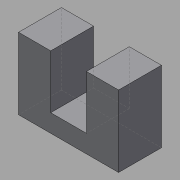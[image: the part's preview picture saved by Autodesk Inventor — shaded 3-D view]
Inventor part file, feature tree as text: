
AUTODESK INVENTOR PART (.ipt)
format: ipt  version: 2015 (Build 190159000, 159)  size: 77,312 bytes
history: native  units: in
note: dims shown in document units (in); Inventor stores cm internally (conversion verified against a paired STEP export)
features: other x3, sketch x2
ambient origin geometry x8: Origin, YZ Plane, XZ Plane, XY Plane, X Axis, Y Axis, Z Axis, Center Point
bodies: Solid1 (feature_tree)
feature tree (5):
  other  "opto_MIR2.ipt"
  other  "Solid1::opto_MIR2.ipt"
  other  "TaggingFeature1"
  sketch  "Sketch1"  dims[d0=0.3937in]
  sketch  "Sketch2"
